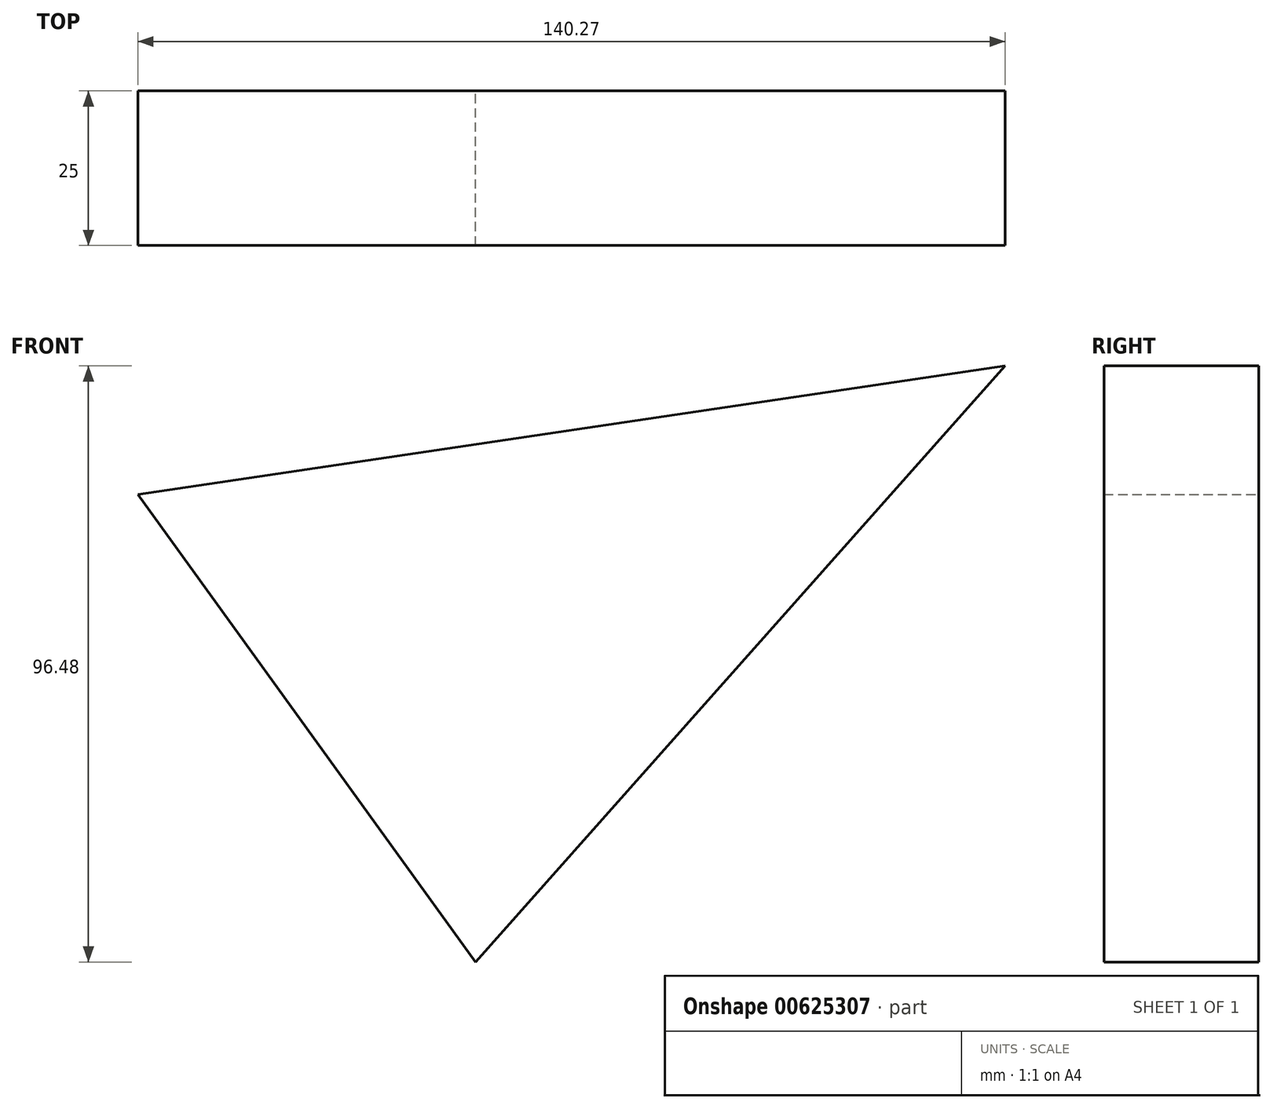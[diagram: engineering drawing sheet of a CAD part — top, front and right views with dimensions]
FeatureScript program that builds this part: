
annotation { "Feature Type Name" : "Feature", "Feature Type Description" : "" }
export const myFeature = defineFeature(function(context is Context, id is Id, definition is map)
    precondition{}
    {
        {
            var Q0;
            Q0=qCreatedBy(makeId("Front.planeOp"),FACE);
            var sketch = newSketch(context, id + "F0", { "sketchPlane" : qUnion([Q0])});
            skLineSegment(sketch, "E0", {"start": v(-54.63, 47.23) * mm, "end": v(0, -28.45) * mm});
            skLineSegment(sketch, "E1", {"start": v(0, -28.45) * mm, "end": v(85.64, 68.03) * mm});
            skLineSegment(sketch, "E2", {"start": v(85.64, 68.03) * mm, "end": v(-54.63, 47.23) * mm});
            skSolve(sketch);
        }
        {
            var Q0;
            Q0=makeQuery(id+"F0.imprint","IMPRINT",FACE,{"disambiguationData":[TD([[makeQuery(id+"F0.imprint","IMPRINT",EDGE,{"derivedFrom":sQuery(id+"F0.wireOp",EDGE,"E0")}),1.0]])]});
            extrude(context, id + "F1", {"entities" : qUnion([Q0]), "depth" : 25 * mm, "offsetDistance" : 25 * mm});
        }
    });
